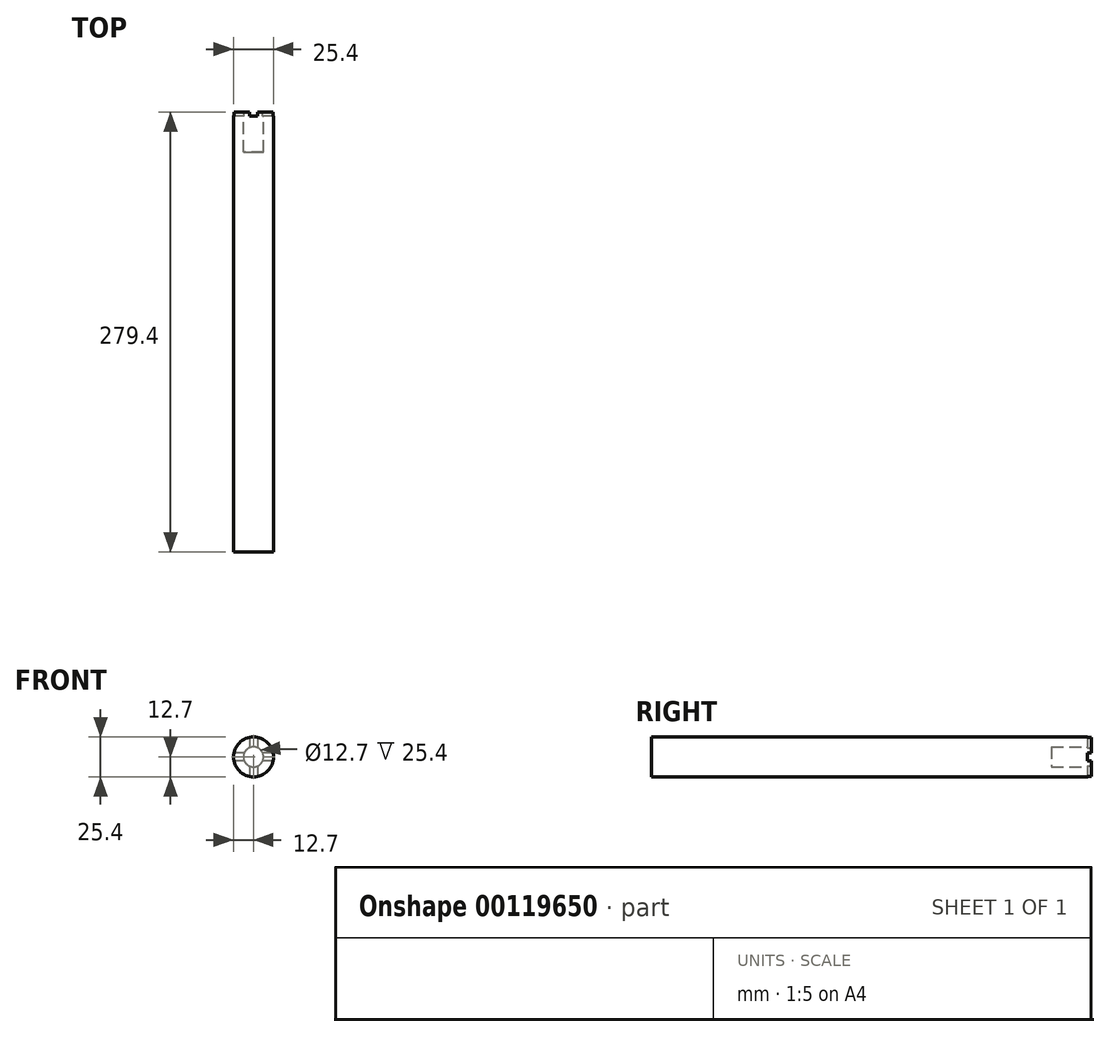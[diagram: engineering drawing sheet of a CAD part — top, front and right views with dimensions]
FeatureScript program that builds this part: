
annotation { "Feature Type Name" : "Feature", "Feature Type Description" : "" }
export const myFeature = defineFeature(function(context is Context, id is Id, definition is map)
    precondition{}
    {
        {
            var Q0;
            Q0=qCreatedBy(makeId("Front.planeOp"),FACE);
            var sketch = newSketch(context, id + "F0", { "sketchPlane" : qUnion([Q0])});
            skCircle(sketch, "E0", {"center": v(0, 0) * mm, "radius": 12.7 * mm});
            skSolve(sketch);
        }
        {
            var Q0;
            Q0 = qSketchRegion(id + "F0", true);
            extrude(context, id + "F1", {"entities" : qUnion([Q0]), "oppositeDirection" : true, "depth" : 279.4 * mm});
        }
        {
            var Q0;
            Q0=makeQuery(id+"F1.opExtrude","CAP_FACE",FACE,{"disambiguationData":[OSD([sQuery(id+"F0.wireOp",EDGE,"E0")])],"isStart":false});
            var sketch = newSketch(context, id + "F2", { "sketchPlane" : qUnion([Q0])});
            skCircle(sketch, "E1", {"center": v(0, 0) * mm, "radius": 6.35 * mm});
            skSolve(sketch);
        }
        {
            var Q0;
            Q0 = qSketchRegion(id + "F2", true);
            extrude(context, id + "F3", {"entities" : qUnion([Q0]), "operationType" : NewBodyOperationType.REMOVE, "oppositeDirection" : true, "depth" : 25.4 * mm});
        }
        {
            var Q0;
            Q0=makeQuery(id+"F1.opExtrude","CAP_FACE",FACE,{"disambiguationData":[OSD([sQuery(id+"F0.wireOp",EDGE,"E0")])],"isStart":false});
            var sketch = newSketch(context, id + "F4", { "sketchPlane" : qUnion([Q0])});
            skLineSegment(sketch, "E2.bottom", {"start": v(-2.54, 19.05) * mm, "end": v(2.54, 19.05) * mm});
            skLineSegment(sketch, "E2.top", {"start": v(-2.54, -19.05) * mm, "end": v(2.54, -19.05) * mm});
            skLineSegment(sketch, "E2.left", {"start": v(-2.54, 19.05) * mm, "end": v(-2.54, -19.05) * mm});
            skLineSegment(sketch, "E2.right", {"start": v(2.54, 19.05) * mm, "end": v(2.54, -19.05) * mm});
            skSolve(sketch);
        }
        {
            var Q0;
            Q0 = qSketchRegion(id + "F4", true);
            extrude(context, id + "F5", {"entities" : qUnion([Q0]), "operationType" : NewBodyOperationType.REMOVE, "oppositeDirection" : true, "depth" : 2.54 * mm});
        }
        {
            var Q0;
            {var subQ0=sQuery(id+"F0.wireOp",EDGE,"E0");Q0=makeQuery(id+"F5.boolean.opBoolean","SPLIT",FACE,{"disambiguationData":[TD([makeQuery(id+"F5.opExtrude","SWEPT_FACE",FACE,{"disambiguationData":[OSD([sQuery(id+"F4.wireOp",EDGE,"E2.left")])]})])],"derivedFrom":makeQuery(id+"F1.opExtrude","CAP_FACE",FACE,{"disambiguationData":[OSD([subQ0])],"isStart":false})});}
            var sketch = newSketch(context, id + "F6", { "sketchPlane" : qUnion([Q0])});
            skLineSegment(sketch, "E3.bottom", {"start": v(-19.05, 2.54) * mm, "end": v(19.05, 2.54) * mm});
            skLineSegment(sketch, "E3.top", {"start": v(-19.05, -2.54) * mm, "end": v(19.05, -2.54) * mm});
            skLineSegment(sketch, "E3.left", {"start": v(-19.05, 2.54) * mm, "end": v(-19.05, -2.54) * mm});
            skLineSegment(sketch, "E3.right", {"start": v(19.05, 2.54) * mm, "end": v(19.05, -2.54) * mm});
            skSolve(sketch);
        }
        {
            var Q0;
            Q0 = qSketchRegion(id + "F6", true);
            extrude(context, id + "F7", {"entities" : qUnion([Q0]), "operationType" : NewBodyOperationType.REMOVE, "oppositeDirection" : true, "depth" : 2.54 * mm});
        }
    });
